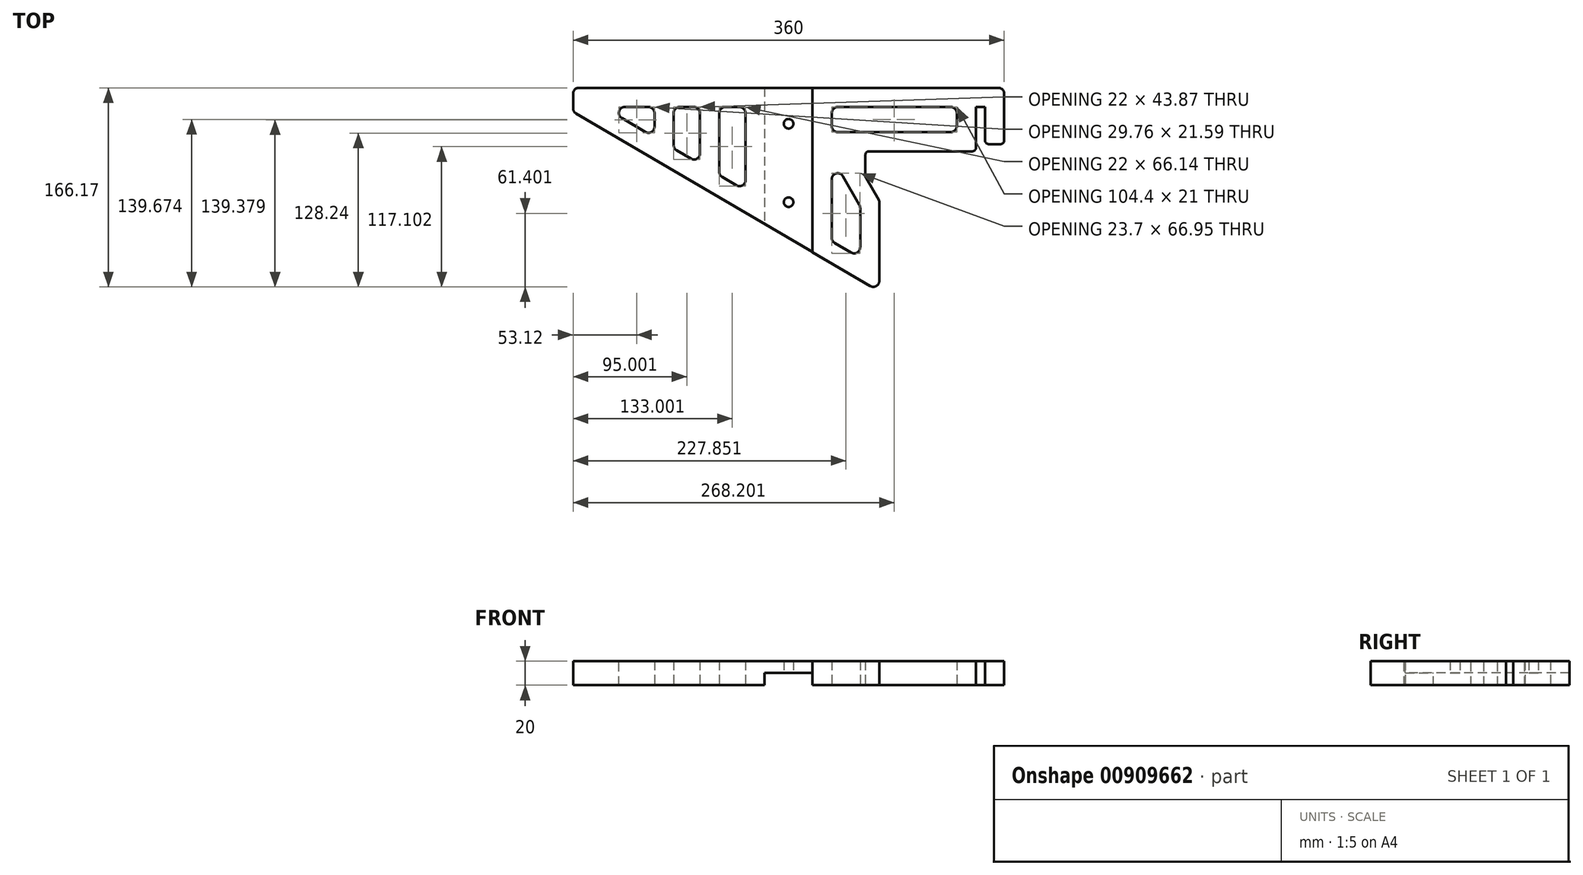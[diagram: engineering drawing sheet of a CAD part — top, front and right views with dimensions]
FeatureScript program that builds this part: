
annotation { "Feature Type Name" : "Feature", "Feature Type Description" : "" }
export const myFeature = defineFeature(function(context is Context, id is Id, definition is map)
    precondition{}
    {
        {
            var Q0;
            Q0=qCreatedBy(makeId("Top.planeOp"),FACE);
            var sketch = newSketch(context, id + "F0", { "sketchPlane" : qUnion([Q0])});
            skLineSegment(sketch, "E0", {"start": v(155.85, 36.64) * mm, "end": v(155.85, -10.36) * mm});
            skLineSegment(sketch, "E1", {"start": v(155.85, -10.36) * mm, "end": v(139.85, -10.36) * mm});
            skLineSegment(sketch, "E2", {"start": v(139.85, -10.36) * mm, "end": v(139.85, 20.64) * mm});
            skLineSegment(sketch, "E3", {"start": v(139.85, 20.64) * mm, "end": v(132.25, 20.64) * mm});
            skLineSegment(sketch, "E4", {"start": v(132.25, 20.64) * mm, "end": v(132.25, -16.36) * mm});
            skLineSegment(sketch, "E5", {"start": v(132.25, -16.36) * mm, "end": v(39.95, -16.36) * mm});
            skLineSegment(sketch, "E6", {"start": v(39.95, -16.36) * mm, "end": v(39.95, -37.66) * mm});
            skLineSegment(sketch, "E7", {"start": v(39.95, -37.66) * mm, "end": v(51.55, -57.75) * mm});
            skLineSegment(sketch, "E8", {"start": v(51.55, -57.75) * mm, "end": v(51.55, -133.26) * mm});
            skLineSegment(sketch, "E9", {"start": v(51.55, -133.26) * mm, "end": v(-204.15, 16.64) * mm});
            skLineSegment(sketch, "E10", {"start": v(-204.15, 36.64) * mm, "end": v(155.85, 36.64) * mm});
            skLineSegment(sketch, "E11", {"start": v(-204.15, 16.64) * mm, "end": v(-204.15, 36.64) * mm});
            skLineSegment(sketch, "E12", {"start": v(-4.15, 36.64) * mm, "end": v(-4.15, -100.6) * mm});
            skLineSegment(sketch, "E13", {"start": v(-44.15, 36.64) * mm, "end": v(-44.15, -77.15) * mm});
            skLineSegment(sketch, "E14", {"start": v(-24.15, 36.64) * mm, "end": v(-24.15, -88.88) * mm});
            skCircle(sketch, "E15", {"center": v(-24.15, 6.64) * mm, "radius": 4 * mm});
            skCircle(sketch, "E16", {"center": v(-24.15, -58.88) * mm, "radius": 4 * mm});
            skLineSegment(sketch, "E17", {"start": v(-60.15, 20.64) * mm, "end": v(-60.15, -49.23) * mm});
            skLineSegment(sketch, "E18", {"start": v(-60.15, -49.23) * mm, "end": v(-179.34, 20.64) * mm});
            skLineSegment(sketch, "E19", {"start": v(-179.34, 20.64) * mm, "end": v(-60.15, 20.64) * mm});
            skLineSegment(sketch, "E20", {"start": v(-82.15, 20.64) * mm, "end": v(-82.15, -36.33) * mm});
            skLineSegment(sketch, "E21", {"start": v(-98.15, 20.64) * mm, "end": v(-98.15, -26.95) * mm});
            skLineSegment(sketch, "E22", {"start": v(116.25, 20.64) * mm, "end": v(116.25, -0.36) * mm});
            skLineSegment(sketch, "E23", {"start": v(116.25, -0.36) * mm, "end": v(11.85, -0.36) * mm});
            skLineSegment(sketch, "E24", {"start": v(11.85, -0.36) * mm, "end": v(11.85, 20.64) * mm});
            skLineSegment(sketch, "E25", {"start": v(11.85, 20.64) * mm, "end": v(116.25, 20.64) * mm});
            skLineSegment(sketch, "E26", {"start": v(11.85, -0.36) * mm, "end": v(11.85, -91.44) * mm});
            skLineSegment(sketch, "E27", {"start": v(11.85, -91.44) * mm, "end": v(35.55, -105.33) * mm});
            skLineSegment(sketch, "E28", {"start": v(35.55, -105.33) * mm, "end": v(35.55, -62.04) * mm});
            skLineSegment(sketch, "E29", {"start": v(35.55, -62.04) * mm, "end": v(11.85, -20.99) * mm});
            skLineSegment(sketch, "E30", {"start": v(-120.15, 20.64) * mm, "end": v(-120.15, -14.05) * mm});
            skLineSegment(sketch, "E31", {"start": v(-136.15, 20.64) * mm, "end": v(-136.15, -4.67) * mm});
            skSolve(sketch);
        }
        {
            var Q0;
            Q0=makeQuery(id+"F0.imprint","IMPRINT",FACE,{"disambiguationData":[TD([[makeQuery(id+"F0.imprint","IMPRINT",EDGE,{"derivedFrom":sQuery(id+"F0.wireOp",EDGE,"E0")}),-1.0]])]});
            extrude(context, id + "F1", {"entities" : qUnion([Q0]), "depth" : 20 * mm, "offsetDistance" : 25 * mm});
        }
        {
            var Q0;
            {var subQ0=sQuery(id+"F0.wireOp",EDGE,"E12");Q0=makeQuery(id+"F0.imprint","IMPRINT",FACE,{"disambiguationData":[TD([[makeQuery(id+"F0.imprint","IMPRINT",EDGE,{"derivedFrom":subQ0}),-1.0]])]});}
            var Q1;
            {var subQ5=sQuery(id+"F0.wireOp",EDGE,"E13");Q1=makeQuery(id+"F0.imprint","IMPRINT",FACE,{"disambiguationData":[TD([[makeQuery(id+"F0.imprint","IMPRINT",EDGE,{"derivedFrom":subQ5}),1.0]])]});}
            extrude(context, id + "F2", {"entities" : qUnion([Q0, Q1]), "operationType" : NewBodyOperationType.ADD, "depth" : 9.9 * mm, "offsetDistance" : 25 * mm});
        }
        {
            var Q0;
            {var subQ0=sQuery(id+"F0.wireOp",EDGE,"E11");Q0=makeQuery(id+"F0.imprint","IMPRINT",FACE,{"disambiguationData":[TD([[makeQuery(id+"F0.imprint","IMPRINT",EDGE,{"derivedFrom":subQ0}),-1.0]])]});}
            var Q1;
            {var subQ0=sQuery(id+"F0.wireOp",EDGE,"E12");Q1=makeQuery(id+"F0.imprint","IMPRINT",FACE,{"disambiguationData":[TD([[makeQuery(id+"F0.imprint","IMPRINT",EDGE,{"derivedFrom":subQ0}),-1.0]])]});}
            var Q2;
            {var subQ5=sQuery(id+"F0.wireOp",EDGE,"E13");Q2=makeQuery(id+"F0.imprint","IMPRINT",FACE,{"disambiguationData":[TD([[makeQuery(id+"F0.imprint","IMPRINT",EDGE,{"derivedFrom":subQ5}),1.0]])]});}
            var Q3;
            {var subQ0=sQuery(id+"F0.wireOp",EDGE,"E30");Q3=makeQuery(id+"F0.imprint","IMPRINT",FACE,{"disambiguationData":[TD([[makeQuery(id+"F0.imprint","IMPRINT",EDGE,{"derivedFrom":subQ0}),-1.0]])]});}
            var Q4;
            {var subQ0=sQuery(id+"F0.wireOp",EDGE,"E20");Q4=makeQuery(id+"F0.imprint","IMPRINT",FACE,{"disambiguationData":[TD([[makeQuery(id+"F0.imprint","IMPRINT",EDGE,{"derivedFrom":subQ0}),-1.0]])]});}
            extrude(context, id + "F3", {"entities" : qUnion([Q0, Q1, Q2, Q3, Q4]), "depth" : 20 * mm, "offsetDistance" : 25 * mm});
        }
        {
            var Q0;
            {var subQ5=sQuery(id+"F0.wireOp",EDGE,"E13");Q0=makeQuery(id+"F0.imprint","IMPRINT",FACE,{"disambiguationData":[TD([[makeQuery(id+"F0.imprint","IMPRINT",EDGE,{"derivedFrom":subQ5}),1.0]])]});}
            var Q1;
            {var subQ0=sQuery(id+"F0.wireOp",EDGE,"E12");Q1=makeQuery(id+"F0.imprint","IMPRINT",FACE,{"disambiguationData":[TD([[makeQuery(id+"F0.imprint","IMPRINT",EDGE,{"derivedFrom":subQ0}),-1.0]])]});}
            extrude(context, id + "F4", {"entities" : qUnion([Q0, Q1]), "operationType" : NewBodyOperationType.REMOVE, "depth" : 10.1 * mm, "offsetDistance" : 25 * mm});
        }
        {
            var Q0;
            Q0=makeQuery(id+"F4.boolean.opBoolean","COPY",FACE,{"derivedFrom":makeQuery(id+"F4.opExtrude","SWEPT_FACE",FACE,{"disambiguationData":[OSD([sQuery(id+"F0.wireOp",EDGE,"E13")])]})});
            var Q1;
            Q1=makeQuery(id+"F3.opExtrude","SWEPT_FACE",FACE,{"disambiguationData":[OSD([sQuery(id+"F0.wireOp",EDGE,"E12")])]});
            extrude(context, id + "F5", {"entities" : qUnion([Q0, Q1]), "operationType" : NewBodyOperationType.REMOVE, "oppositeDirection" : true, "depth" : .2 * mm, "offsetDistance" : 25 * mm});
        }
        {
            var Q0;
            Q0=makeQuery(id+"F3.opExtrude","SWEPT_EDGE",EDGE,{"disambiguationData":[OSD([sQuery(id+"F0.wireOp",EDGE,"E18"),sQuery(id+"F0.wireOp",EDGE,"E19")])]});
            var Q1;
            Q1=makeQuery(id+"F3.opExtrude","SWEPT_EDGE",EDGE,{"disambiguationData":[OSD([sQuery(id+"F0.wireOp",EDGE,"E19"),sQuery(id+"F0.wireOp",EDGE,"E31")])]});
            var Q2;
            Q2=makeQuery(id+"F3.opExtrude","SWEPT_EDGE",EDGE,{"disambiguationData":[OSD([sQuery(id+"F0.wireOp",EDGE,"E18"),sQuery(id+"F0.wireOp",EDGE,"E31")])]});
            var Q3;
            Q3=makeQuery(id+"F3.opExtrude","SWEPT_EDGE",EDGE,{"disambiguationData":[OSD([sQuery(id+"F0.wireOp",EDGE,"E18"),sQuery(id+"F0.wireOp",EDGE,"E21")])]});
            var Q4;
            Q4=makeQuery(id+"F3.opExtrude","SWEPT_EDGE",EDGE,{"disambiguationData":[OSD([sQuery(id+"F0.wireOp",EDGE,"E19"),sQuery(id+"F0.wireOp",EDGE,"E21")])]});
            var Q5;
            Q5=makeQuery(id+"F3.opExtrude","SWEPT_EDGE",EDGE,{"disambiguationData":[OSD([sQuery(id+"F0.wireOp",EDGE,"E19"),sQuery(id+"F0.wireOp",EDGE,"E30")])]});
            var Q6;
            Q6=makeQuery(id+"F3.opExtrude","SWEPT_EDGE",EDGE,{"disambiguationData":[OSD([sQuery(id+"F0.wireOp",EDGE,"E18"),sQuery(id+"F0.wireOp",EDGE,"E30")])]});
            var Q7;
            Q7=makeQuery(id+"F3.opExtrude","SWEPT_EDGE",EDGE,{"disambiguationData":[OSD([sQuery(id+"F0.wireOp",EDGE,"E17"),sQuery(id+"F0.wireOp",EDGE,"E19")])]});
            var Q8;
            Q8=makeQuery(id+"F3.opExtrude","SWEPT_EDGE",EDGE,{"disambiguationData":[OSD([sQuery(id+"F0.wireOp",EDGE,"E17"),sQuery(id+"F0.wireOp",EDGE,"E18")])]});
            var Q9;
            Q9=makeQuery(id+"F3.opExtrude","SWEPT_EDGE",EDGE,{"disambiguationData":[OSD([sQuery(id+"F0.wireOp",EDGE,"E18"),sQuery(id+"F0.wireOp",EDGE,"E20")])]});
            var Q10;
            Q10=makeQuery(id+"F3.opExtrude","SWEPT_EDGE",EDGE,{"disambiguationData":[OSD([sQuery(id+"F0.wireOp",EDGE,"E19"),sQuery(id+"F0.wireOp",EDGE,"E20")])]});
            var Q11;
            Q11=makeQuery(id+"F1.opExtrude","SWEPT_EDGE",EDGE,{"disambiguationData":[OSD([sQuery(id+"F0.wireOp",EDGE,"E27"),sQuery(id+"F0.wireOp",EDGE,"E28")])]});
            var Q12;
            Q12=makeQuery(id+"F1.opExtrude","SWEPT_EDGE",EDGE,{"disambiguationData":[OSD([sQuery(id+"F0.wireOp",EDGE,"E26"),sQuery(id+"F0.wireOp",EDGE,"E27")])]});
            var Q13;
            Q13=makeQuery(id+"F1.opExtrude","SWEPT_EDGE",EDGE,{"disambiguationData":[OSD([sQuery(id+"F0.wireOp",EDGE,"E26"),sQuery(id+"F0.wireOp",EDGE,"E29")])]});
            var Q14;
            Q14=makeQuery(id+"F1.opExtrude","SWEPT_EDGE",EDGE,{"disambiguationData":[OSD([sQuery(id+"F0.wireOp",EDGE,"E28"),sQuery(id+"F0.wireOp",EDGE,"E29")])]});
            var Q15;
            Q15=makeQuery(id+"F1.opExtrude","SWEPT_EDGE",EDGE,{"disambiguationData":[OSD([sQuery(id+"F0.wireOp",EDGE,"E24"),sQuery(id+"F0.wireOp",EDGE,"E25")])]});
            var Q16;
            Q16=makeQuery(id+"F1.opExtrude","SWEPT_EDGE",EDGE,{"disambiguationData":[OSD([sQuery(id+"F0.wireOp",EDGE,"E23"),sQuery(id+"F0.wireOp",EDGE,"E24")])]});
            var Q17;
            Q17=makeQuery(id+"F1.opExtrude","SWEPT_EDGE",EDGE,{"disambiguationData":[OSD([sQuery(id+"F0.wireOp",EDGE,"E22"),sQuery(id+"F0.wireOp",EDGE,"E23")])]});
            var Q18;
            Q18=makeQuery(id+"F1.opExtrude","SWEPT_EDGE",EDGE,{"disambiguationData":[OSD([sQuery(id+"F0.wireOp",EDGE,"E22"),sQuery(id+"F0.wireOp",EDGE,"E25")])]});
            var Q19;
            Q19=makeQuery(id+"F1.opExtrude","SWEPT_EDGE",EDGE,{"disambiguationData":[OSD([sQuery(id+"F0.wireOp",EDGE,"E0"),sQuery(id+"F0.wireOp",EDGE,"E10")])]});
            var Q20;
            Q20=makeQuery(id+"F1.opExtrude","SWEPT_EDGE",EDGE,{"disambiguationData":[OSD([sQuery(id+"F0.wireOp",EDGE,"E8"),sQuery(id+"F0.wireOp",EDGE,"E9")])]});
            var Q21;
            Q21=makeQuery(id+"F3.opExtrude","SWEPT_EDGE",EDGE,{"disambiguationData":[OSD([sQuery(id+"F0.wireOp",EDGE,"E9"),sQuery(id+"F0.wireOp",EDGE,"E11")])]});
            var Q22;
            Q22=makeQuery(id+"F3.opExtrude","SWEPT_EDGE",EDGE,{"disambiguationData":[OSD([sQuery(id+"F0.wireOp",EDGE,"E10"),sQuery(id+"F0.wireOp",EDGE,"E11")])]});
            fillet(context, id + "F6", {"entities" : qUnion([Q0, Q1, Q2, Q3, Q4, Q5, Q6, Q7, Q8, Q9, Q10, Q11, Q12, Q13, Q14, Q15, Q16, Q17, Q18, Q19, Q20, Q21, Q22]), "radius" : 5 * mm, "tangentPropagation" : true, "allowEdgeOverflow" : false});
        }
        {
            var Q0;
            Q0=makeQuery(id+"F1.opExtrude","SWEPT_EDGE",EDGE,{"disambiguationData":[OSD([sQuery(id+"F0.wireOp",EDGE,"E4"),sQuery(id+"F0.wireOp",EDGE,"E5")])]});
            var Q1;
            Q1=makeQuery(id+"F1.opExtrude","SWEPT_EDGE",EDGE,{"disambiguationData":[OSD([sQuery(id+"F0.wireOp",EDGE,"E1"),sQuery(id+"F0.wireOp",EDGE,"E2")])]});
            var Q2;
            Q2=makeQuery(id+"F1.opExtrude","SWEPT_EDGE",EDGE,{"disambiguationData":[OSD([sQuery(id+"F0.wireOp",EDGE,"E0"),sQuery(id+"F0.wireOp",EDGE,"E1")])]});
            var Q3;
            Q3=makeQuery(id+"F1.opExtrude","SWEPT_EDGE",EDGE,{"disambiguationData":[OSD([sQuery(id+"F0.wireOp",EDGE,"E8"),sQuery(id+"F0.wireOp",EDGE,"E9")])]});
            var Q4;
            Q4=makeQuery(id+"F1.opExtrude","SWEPT_EDGE",EDGE,{"disambiguationData":[OSD([sQuery(id+"F0.wireOp",EDGE,"E7"),sQuery(id+"F0.wireOp",EDGE,"E8")])]});
            var Q5;
            Q5=makeQuery(id+"F1.opExtrude","SWEPT_EDGE",EDGE,{"disambiguationData":[OSD([sQuery(id+"F0.wireOp",EDGE,"E6"),sQuery(id+"F0.wireOp",EDGE,"E7")])]});
            var Q6;
            Q6=makeQuery(id+"F1.opExtrude","SWEPT_EDGE",EDGE,{"disambiguationData":[OSD([sQuery(id+"F0.wireOp",EDGE,"E5"),sQuery(id+"F0.wireOp",EDGE,"E6")])]});
            fillet(context, id + "F7", {"entities" : qUnion([Q0, Q1, Q2, Q3, Q4, Q5, Q6]), "radius" : 3 * mm, "tangentPropagation" : true, "allowEdgeOverflow" : false});
        }
    });
